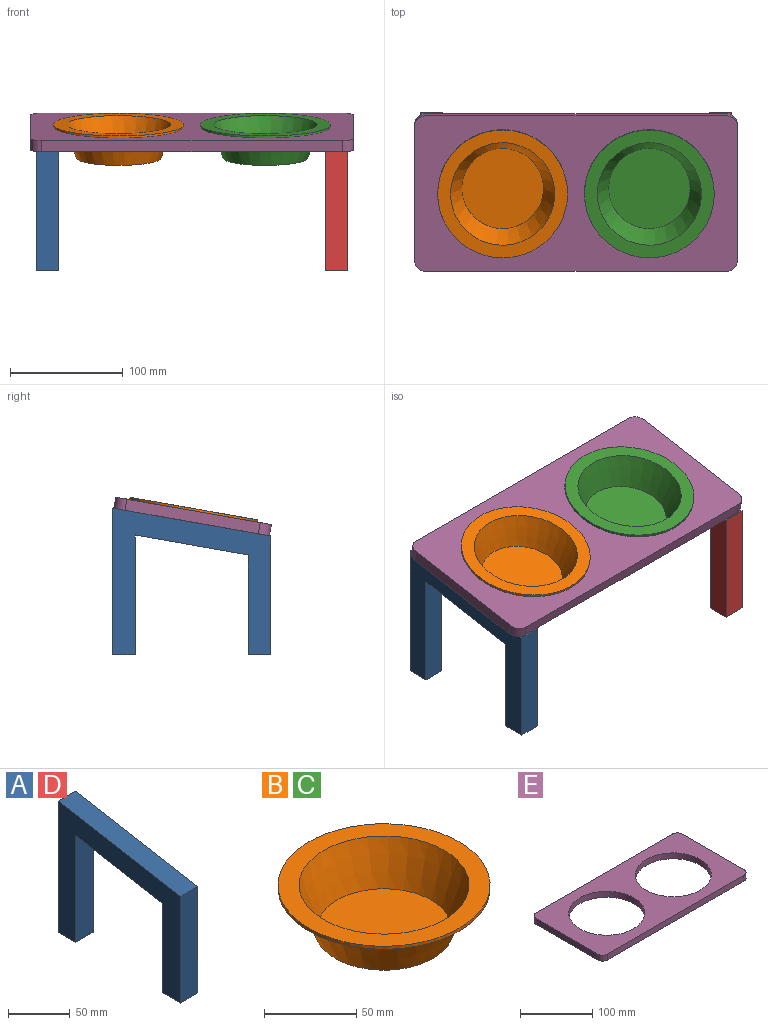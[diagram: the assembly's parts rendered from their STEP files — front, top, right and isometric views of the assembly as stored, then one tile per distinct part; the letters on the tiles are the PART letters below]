
ASSEMBLY  parts=5 mates=4
PART A: 10 faces, bbox 20x140x130 mm
  f0: plane 140x130mm, normal (1,0,0), area 6737.1mm2, adj f2,f3,f4,f5,f6,f7,f8,f9
  f1: plane 140x130mm, normal (-1,0,0), area 6737.1mm2, adj f2,f3,f4,f5,f6,f7,f8,f9
  f2: plane 20x20mm, normal (0,0,-1), area 400mm2, adj f0,f1,f5,f8
  f3: plane 105.31x20mm, normal (0,-1,0), area 2106.3mm2, adj f0,f1,f4,f6
  f4: plane 20x20mm, normal (0,0,-1), area 400mm2, adj f0,f1,f3,f7
  f5: plane 130x20mm, normal (0,1,0), area 2600mm2, adj f0,f1,f2,f6
  f6: plane 140x24.69mm, normal (0,-0.17,0.98), area 2843.2mm2, adj f0,f1,f3,f5
  f7: plane 88.53x20mm, normal (0,1,0), area 1770.6mm2, adj f0,f1,f4,f9
  f8: plane 106.17x20mm, normal (0,-1,0), area 2123.3mm2, adj f0,f1,f2,f9
  f9: plane 100x20mm, normal (0,0.17,-0.98), area 2030.9mm2, adj f0,f1,f7,f8
PART B: 7 faces, bbox 115x115x30 mm
  f0: cylinder r=57.5mm len=115mm, axis (0,0,1), area 722.6mm2, adj f1,f2
  f1: plane 115x115mm, normal (0,0,1), area 3713.1mm2, adj f0,f5
  f2: plane 115x115mm, normal (0,0,-1), area 3298.7mm2, adj f0,f3
  f3: cone r=47.5mm half-angle=19.7deg, axis (0,0,1), area 7939.5mm2, adj f2,f4
  f4: plane 75x75mm, normal (0,0,-1), area 4417.9mm2, adj f3
  f5: cone r=45.62mm half-angle=19.7deg, axis (0,0,1), area 7676.2mm2, adj f1,f6
  f6: plane 72.18x72.18mm, normal (0,0,1), area 4092mm2, adj f5
PART C: same geometry as B
PART D: same geometry as A
PART E: 12 faces, bbox 286x140x10 mm
  f0: plane 286x140mm, normal (0,0,1), area 22636.1mm2, adj f2,f3,f4,f5,f6,f7,f8,f9
  f1: plane 286x140mm, normal (0,0,-1), area 22636.1mm2, adj f2,f3,f4,f5,f6,f7,f8,f9
  f2: cylinder r=10mm len=10mm, axis (0,0,1), area 157.1mm2, adj f0,f1,f3,f9
  f3: plane 266x10mm, normal (0,1,0), area 2660mm2, adj f0,f1,f2,f4
  f4: cylinder r=10mm len=10mm, axis (0,0,1), area 157.1mm2, adj f0,f1,f3,f5
  f5: plane 120x10mm, normal (1,0,0), area 1200mm2, adj f0,f1,f4,f6
  f6: cylinder r=10mm len=10mm, axis (0,0,1), area 157.1mm2, adj f0,f1,f5,f7
  f7: plane 266x10mm, normal (0,-1,0), area 2660mm2, adj f0,f1,f6,f8
  f8: cylinder r=10mm len=10mm, axis (0,0,1), area 157.1mm2, adj f0,f1,f7,f9
  f9: plane 120x10mm, normal (-1,0,0), area 1200mm2, adj f0,f1,f2,f8
  f10: cylinder r=52.5mm len=105mm, axis (0,0,1), area 3298.7mm2, adj f0,f1
  f11: cylinder r=52.5mm len=105mm, axis (0,0,1), area 3298.7mm2, adj f0,f1
PLACE A t=(-484,70,142)mm
PLACE B rot(axis=(1,0,0),10deg) t=(-203,47.92,129.47)mm
PLACE C rot(axis=(1,0,0),10deg) t=(-73,47.92,129.47)mm
PLACE D t=(-228,70,142)mm
PLACE E rot(axis=(1,0,0),10deg) t=(-203,47.92,129.47)mm
MATE fastened B.f0 <-> E.f11  axis (0,0.17,-0.98) through (-203,48.26,127.51)mm
MATE fastened A.f6 <-> E.f1  axis (0,-0.17,0.98) through (-276,50,117.66)mm
MATE fastened C.f0 <-> E.f10  axis (0,0.17,-0.98) through (-73,48.26,127.51)mm
MATE fastened E.f1 <-> D.f6  axis (0,0.17,-0.98) through (5,50,117.66)mm
